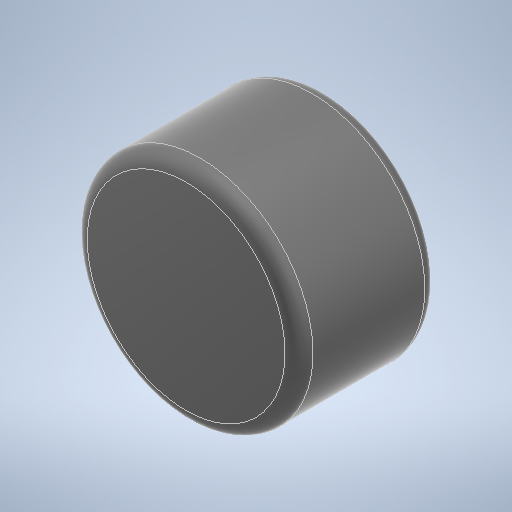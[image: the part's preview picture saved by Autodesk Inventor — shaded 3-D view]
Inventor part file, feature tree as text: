
AUTODESK INVENTOR PART (.ipt)
format: ipt  version: 2025.1 (Build 291241020, 241B)  size: 605,184 bytes
history: native  units: mm
features: revolve x1, fillet x1, sketch x1
ambient origin geometry x8: Origin, YZ Plane, XZ Plane, XY Plane, X Axis, Y Axis, Z Axis, Center Point
bodies: Solid1 (feature_tree)
feature tree (3):
  revolve  "Revolution1"  [1 undecoded]
  fillet  "Fillet1"  Radius=20.0mm
  sketch  "Sketch1"  dims[d0=16.15mm d1=10.2mm d2=20.0mm d3=5.0mm d4=360.0deg d5=2.0mm]
note: 1 required parameter value undecoded (feature->parameter linkage not recoverable at this tier; creation-order binding heuristic only, values carry confidence <= 0.55)
